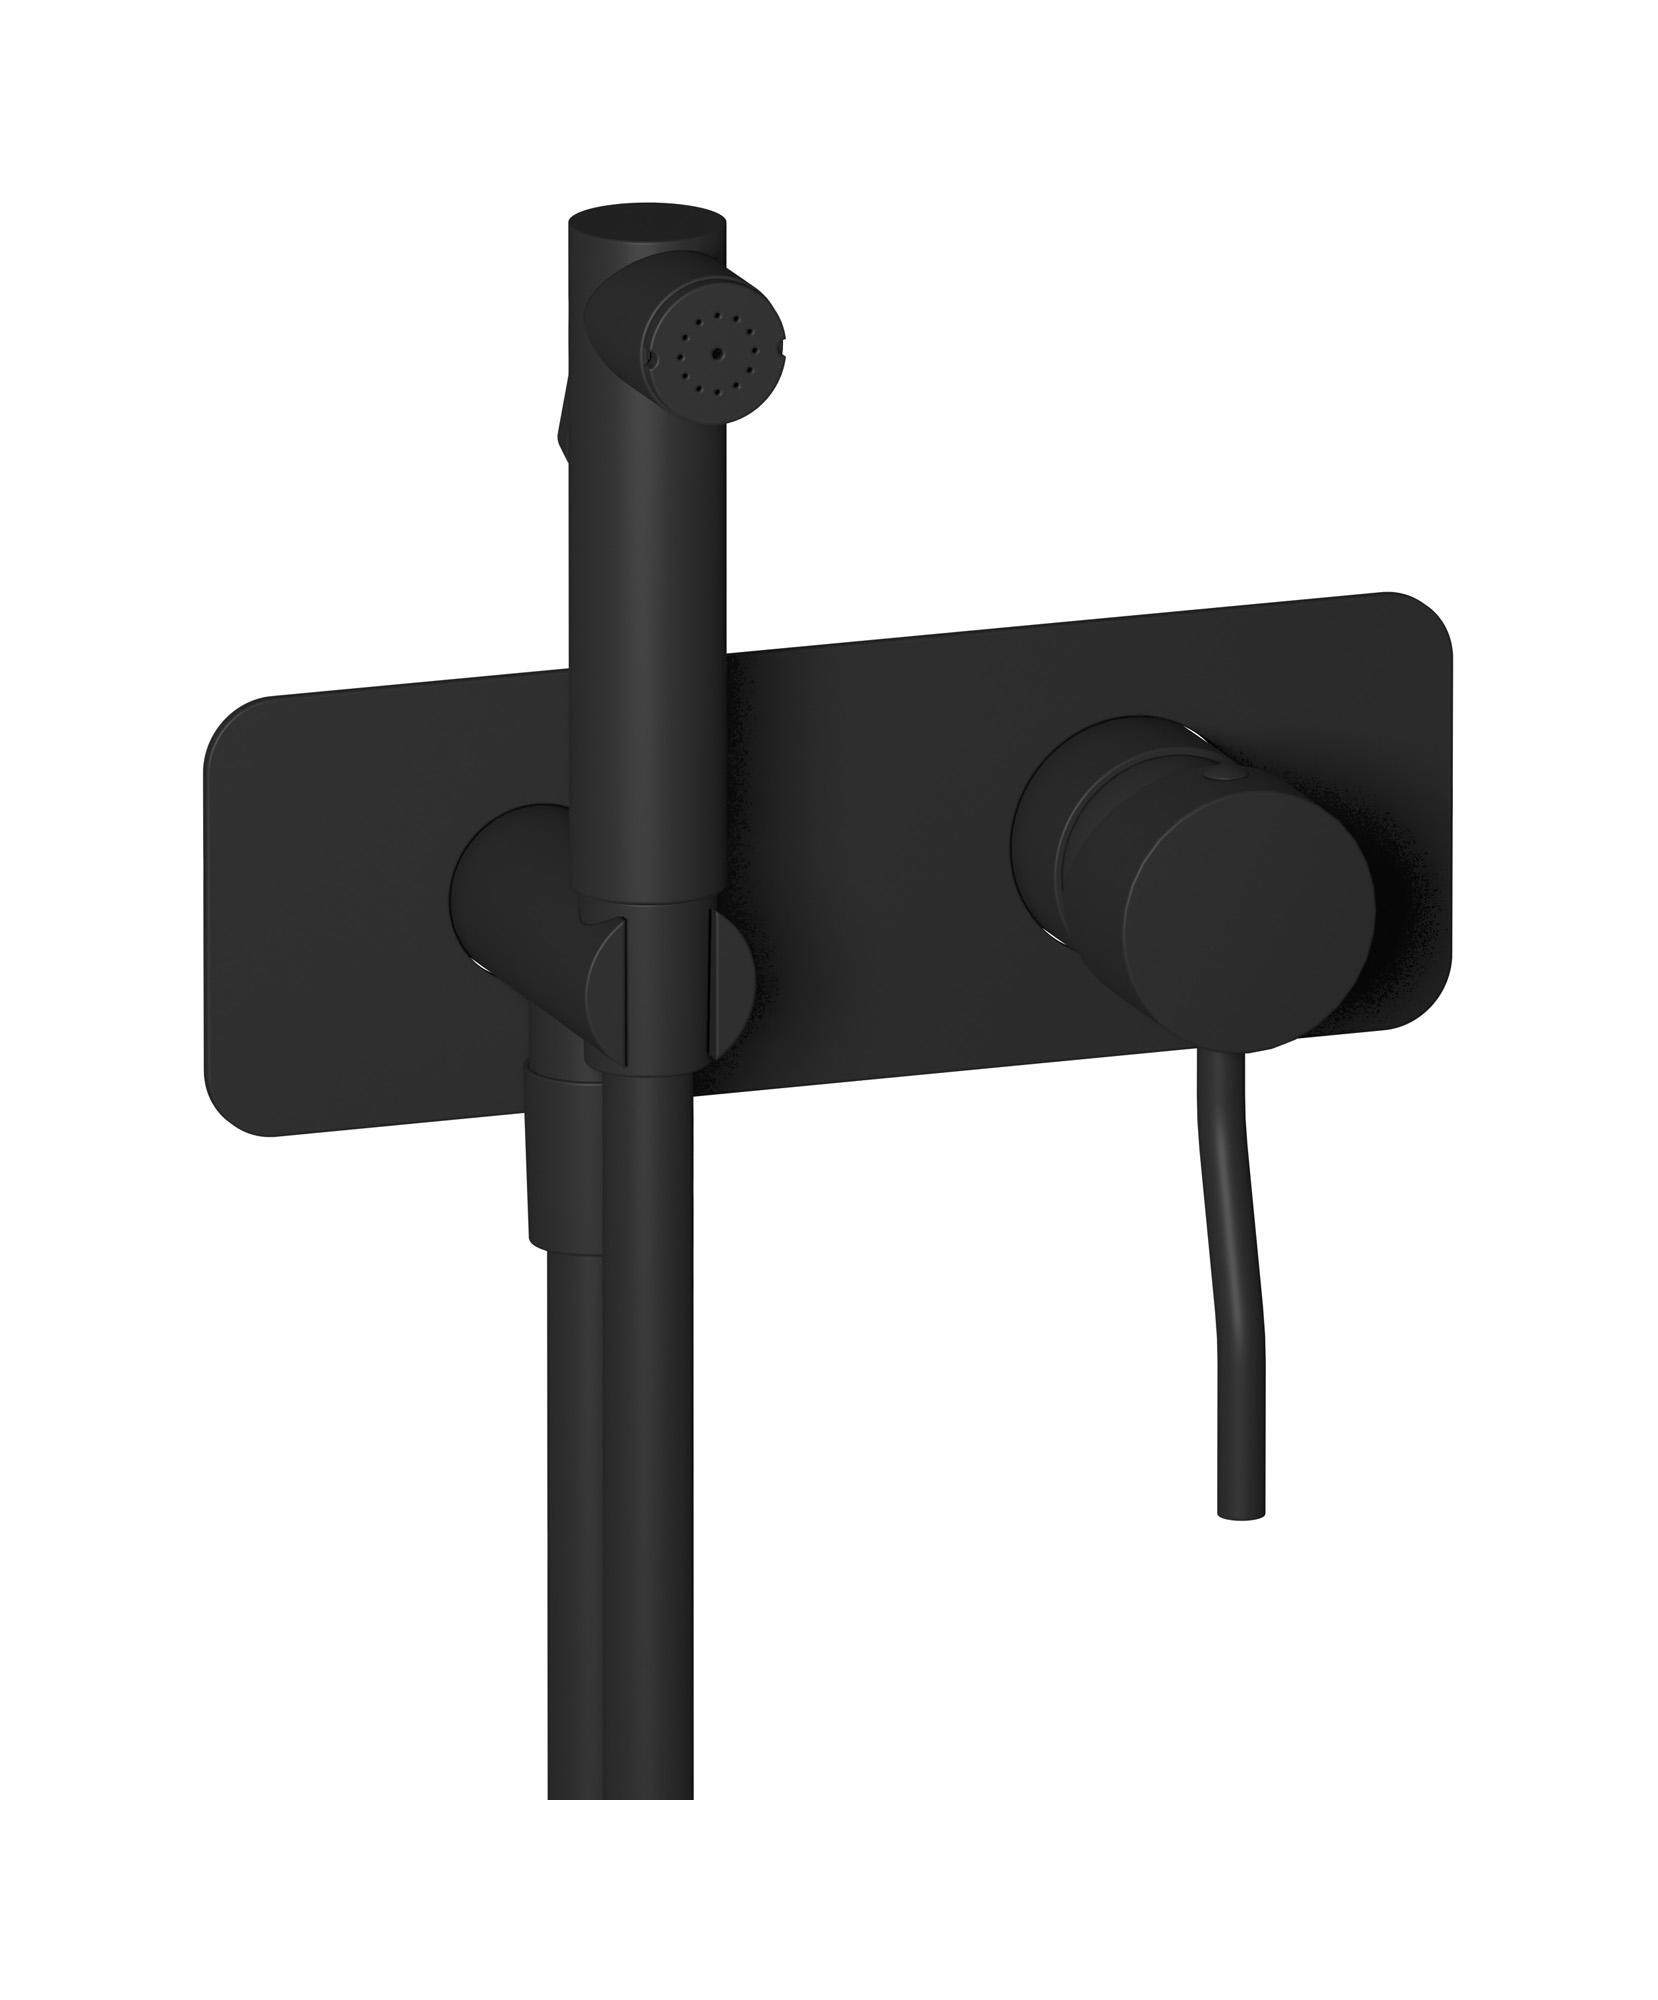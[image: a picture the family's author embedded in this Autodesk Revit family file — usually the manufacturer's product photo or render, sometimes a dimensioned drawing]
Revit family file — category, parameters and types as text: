
# Revit family: KU706
name_source: partatom
category: Apparecchi idraulici
units: mm (PartAtom-declared; Revit-internal decimal feet)

## family parameters
Basato su piano di lavoro = No
Condiviso = No
Mantieni orientamento annotazione = No
Numero OmniClass = 23.45.55.17
Punto di calcolo locali = No
Quota connettore circolare = Usa diametro
Sempre verticale = Sì
Taglio con vuoti quando caricato = No
Tipo di parte = Normale
Titolo OmniClass = Mixing Faucets

## types (3) — shared parameters
Cold water inlet = 10 mm  [stored 0.0328084 ft]
Commenti sul tipo = Exposed parts for bidet spray complete with mixer
Connessione CW = No
Connessione HW = No
Connessione di scarico = No
Connessione di ventilazione = No
Descrizione = Exposed parts for bidet spray complete with mixer
Hot water inlet = 10 mm  [stored 0.0328084 ft]
Produttore = IB Rubinetterie S.p.A.
URL = https://www.weareib.it
zero-valued in all types: Prospetto di default

## per-type parameters (varying)
| type | Finishes surface | Immagine tipo | Modello |
| Chrome | IB_Chrome | KU706CC.jpg | KU706CC |
| Matt Black | IB_matt black | KU706NP.jpg | KU706NP |
| Brushed Nickel | IB_Brushed nickel | KU706SS.jpg | KU706SS |

note: [stored X ft] marks values corroborated as IEEE doubles in the binary element streams (Revit-internal decimal feet)
